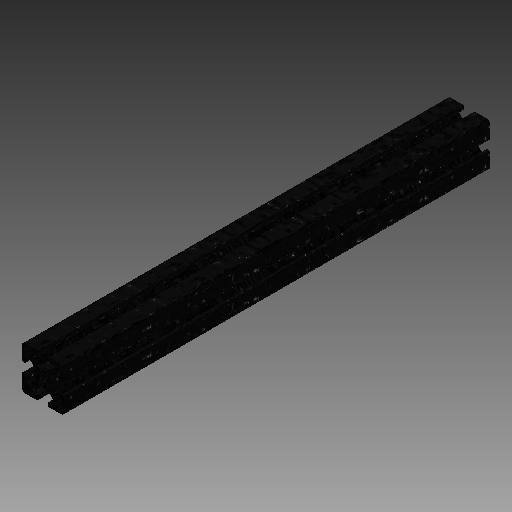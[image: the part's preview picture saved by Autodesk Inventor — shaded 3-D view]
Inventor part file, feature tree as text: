
AUTODESK INVENTOR PART (.ipt)
format: ipt  version: 2019 (Build 230136000, 136)  size: 265,728 bytes
history: native  units: in
note: dims shown in document units (in); Inventor stores cm internally (conversion verified against a paired STEP export)
features: plane x1, extrude x1, sketch x1
ambient origin geometry x8: Origin, YZ Plane, XZ Plane, XY Plane, X Axis, Y Axis, Z Axis, Center Point
bodies: Solid1 (feature_tree)
feature tree (3):
  plane  "Work Plane1"
  extrude  "Extrusion1"  [1 undecoded]
  sketch  "Sketch1"  dims[d0=14.75in d1=0.0in]
note: 1 required parameter value undecoded (feature->parameter linkage not recoverable at this tier; creation-order binding heuristic only, values carry confidence <= 0.55)
